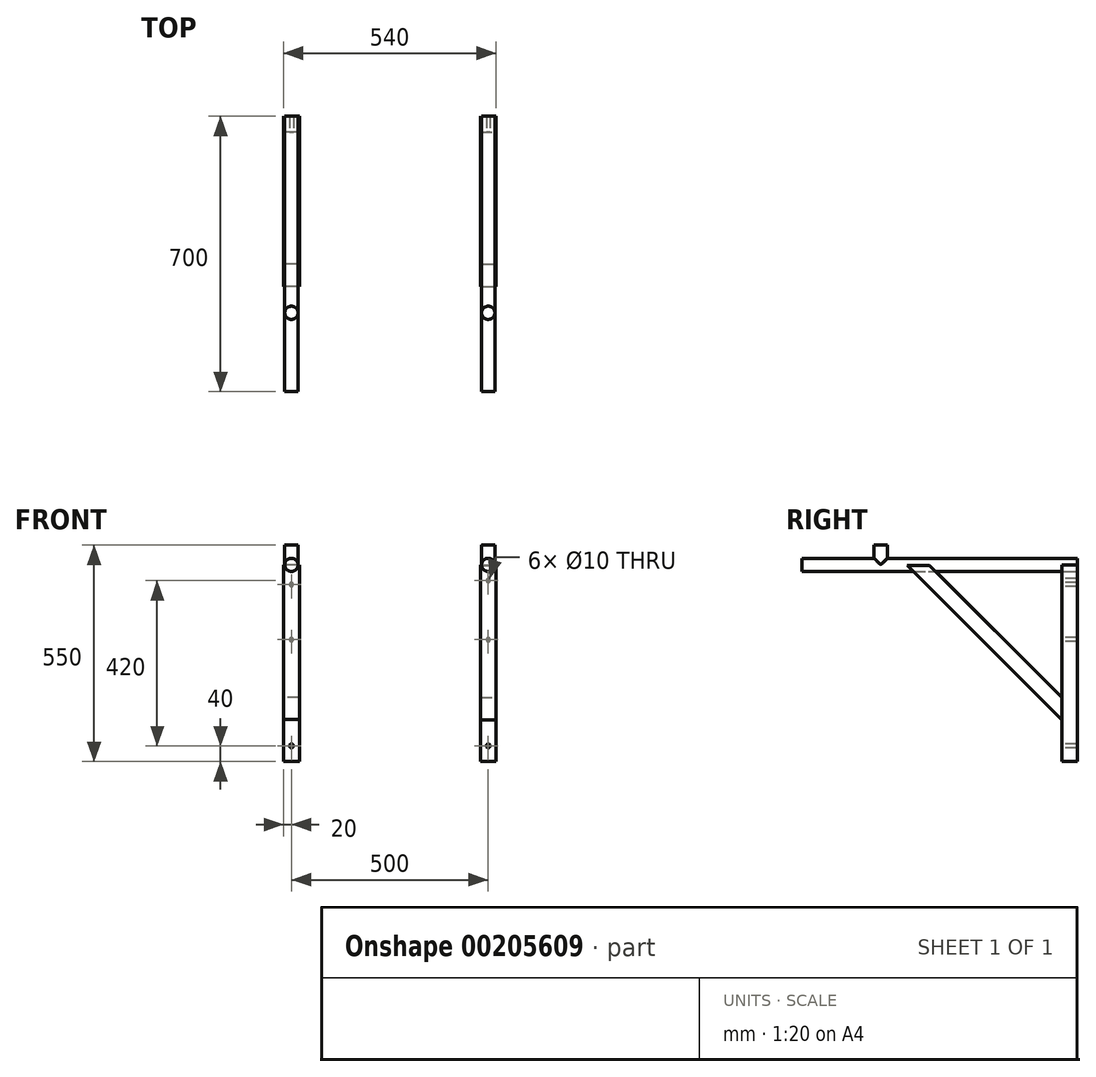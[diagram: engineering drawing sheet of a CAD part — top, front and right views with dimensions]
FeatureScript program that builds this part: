
annotation { "Feature Type Name" : "Feature", "Feature Type Description" : "" }
export const myFeature = defineFeature(function(context is Context, id is Id, definition is map)
    precondition{}
    {
        {
            var Q0;
            Q0=qCreatedBy(makeId("Front.planeOp"),FACE);
            var sketch = newSketch(context, id + "F0", { "sketchPlane" : qUnion([Q0])});
            skCircle(sketch, "E0", {"center": v(-250, 0) * mm, "radius": 16.85 * mm});
            skCircle(sketch, "E1", {"center": v(250, 0) * mm, "radius": 16.85 * mm});
            skSolve(sketch);
        }
        {
            var Q0;
            Q0 = qSketchRegion(id + "F0", true);
            extrude(context, id + "F1", {"entities" : qUnion([Q0]), "depth" : (500 + 200) * mm});
        }
        {
            var Q0;
            Q0=qCreatedBy(makeId("Top.planeOp"),FACE);
            var sketch = newSketch(context, id + "F2", { "sketchPlane" : qUnion([Q0])});
            skCircle(sketch, "E2", {"center": v(-250.04, -499.7) * mm, "radius": 16.85 * mm});
            skCircle(sketch, "E3", {"center": v(249.96, -499.7) * mm, "radius": 16.85 * mm});
            skSolve(sketch);
        }
        {
            var Q0;
            Q0 = qSketchRegion(id + "F2", true);
            extrude(context, id + "F3", {"entities" : qUnion([Q0]), "operationType" : NewBodyOperationType.ADD, "depth" : 50 * mm});
        }
        {
            var Q0;
            Q0=qCreatedBy(makeId("Top.planeOp"),FACE);
            var sketch = newSketch(context, id + "F4", { "sketchPlane" : qUnion([Q0])});
            skLineSegment(sketch, "E4.bottom", {"start": v(-230, 0) * mm, "end": v(-270, 0) * mm});
            skLineSegment(sketch, "E4.top", {"start": v(-230, -40) * mm, "end": v(-270, -40) * mm});
            skLineSegment(sketch, "E4.left", {"start": v(-230, 0) * mm, "end": v(-230, -40) * mm});
            skLineSegment(sketch, "E4.right", {"start": v(-270, 0) * mm, "end": v(-270, -40) * mm});
            skLineSegment(sketch, "E5.bottom", {"start": v(230, 0) * mm, "end": v(270, 0) * mm});
            skLineSegment(sketch, "E5.top", {"start": v(230, -40) * mm, "end": v(270, -40) * mm});
            skLineSegment(sketch, "E5.left", {"start": v(230, 0) * mm, "end": v(230, -40) * mm});
            skLineSegment(sketch, "E5.right", {"start": v(270, 0) * mm, "end": v(270, -40) * mm});
            skSolve(sketch);
        }
        {
            var Q0;
            Q0 = qSketchRegion(id + "F4", true);
            extrude(context, id + "F5", {"entities" : qUnion([Q0]), "oppositeDirection" : true, "depth" : 500 * mm});
        }
        {
            var Q0;
            Q0=makeQuery(id+"F5.opExtrude","SWEPT_FACE",FACE,{"disambiguationData":[OSD([sQuery(id+"F4.wireOp",EDGE,"E4.right")])]});
            var sketch = newSketch(context, id + "F6", { "sketchPlane" : qUnion([Q0])});
            skLineSegment(sketch, "E6", {"start": v(40, -336.36) * mm, "end": v(376.36, 0) * mm});
            skLineSegment(sketch, "E7", {"start": v(376.36, 0) * mm, "end": v(432.92, 0) * mm});
            skLineSegment(sketch, "E8", {"start": v(432.92, 0) * mm, "end": v(40, -392.92) * mm});
            skLineSegment(sketch, "E9", {"start": v(40, -392.92) * mm, "end": v(40, -336.36) * mm});
            skSolve(sketch);
        }
        {
            var Q0;
            Q0 = qSketchRegion(id + "F6", true);
            extrude(context, id + "F7", {"entities" : qUnion([Q0]), "oppositeDirection" : true, "depth" : 40 * mm});
        }
        {
            var Q0;
            Q0=makeQuery(id+"F5.opExtrude","SWEPT_FACE",FACE,{"disambiguationData":[OSD([sQuery(id+"F4.wireOp",EDGE,"E5.right")])]});
            var sketch = newSketch(context, id + "F8", { "sketchPlane" : qUnion([Q0])});
            skLineSegment(sketch, "E10", {"start": v(-40, -336.9) * mm, "end": v(-375.88, -1.02) * mm});
            skLineSegment(sketch, "E11", {"start": v(-375.88, -1.02) * mm, "end": v(-432.44, -1.02) * mm});
            skLineSegment(sketch, "E12", {"start": v(-432.44, -1.02) * mm, "end": v(-40, -393.46) * mm});
            skLineSegment(sketch, "E13", {"start": v(-40, -393.46) * mm, "end": v(-40, -336.9) * mm});
            skSolve(sketch);
        }
        {
            var Q0;
            Q0 = qSketchRegion(id + "F8", true);
            extrude(context, id + "F9", {"entities" : qUnion([Q0]), "oppositeDirection" : true, "depth" : 40 * mm});
        }
        {
            var Q0;
            Q0=makeQuery(id+"F5.opExtrude","SWEPT_FACE",FACE,{"disambiguationData":[OSD([sQuery(id+"F4.wireOp",EDGE,"E4.top")])]});
            var sketch = newSketch(context, id + "F10", { "sketchPlane" : qUnion([Q0])});
            skCircle(sketch, "E14", {"center": v(-250, -50) * mm, "radius": 5 * mm});
            skPoint(sketch, "E14.centerSnap0", {"position": v(-250, 0) * mm});
            skCircle(sketch, "E15", {"center": v(-250, -190) * mm, "radius": 5 * mm});
            skCircle(sketch, "E16", {"center": v(-250, -460) * mm, "radius": 5 * mm});
            skPoint(sketch, "E16.centerSnap0", {"position": v(-250, -500) * mm});
            skSolve(sketch);
        }
        {
            var Q0;
            Q0 = qSketchRegion(id + "F10", true);
            extrude(context, id + "F11", {"entities" : qUnion([Q0]), "operationType" : NewBodyOperationType.REMOVE, "endBound" : BoundingType.THROUGH_ALL, "oppositeDirection" : true, "depth" : 25 * mm});
        }
        {
            var Q0;
            Q0=makeQuery(id+"F5.opExtrude","SWEPT_FACE",FACE,{"disambiguationData":[OSD([sQuery(id+"F4.wireOp",EDGE,"E5.top")])]});
            var sketch = newSketch(context, id + "F12", { "sketchPlane" : qUnion([Q0])});
            skCircle(sketch, "E17", {"center": v(250, -40) * mm, "radius": 5 * mm});
            skPoint(sketch, "E17.centerSnap0", {"position": v(250, 0) * mm});
            skCircle(sketch, "E18", {"center": v(250, -190) * mm, "radius": 5 * mm});
            skCircle(sketch, "E19", {"center": v(250, -460) * mm, "radius": 5 * mm});
            skPoint(sketch, "E19.centerSnap0", {"position": v(250, -500) * mm});
            skSolve(sketch);
        }
        {
            var Q0;
            Q0 = qSketchRegion(id + "F12", true);
            extrude(context, id + "F13", {"entities" : qUnion([Q0]), "operationType" : NewBodyOperationType.REMOVE, "endBound" : BoundingType.THROUGH_ALL, "oppositeDirection" : true, "depth" : 25 * mm});
        }
    });
